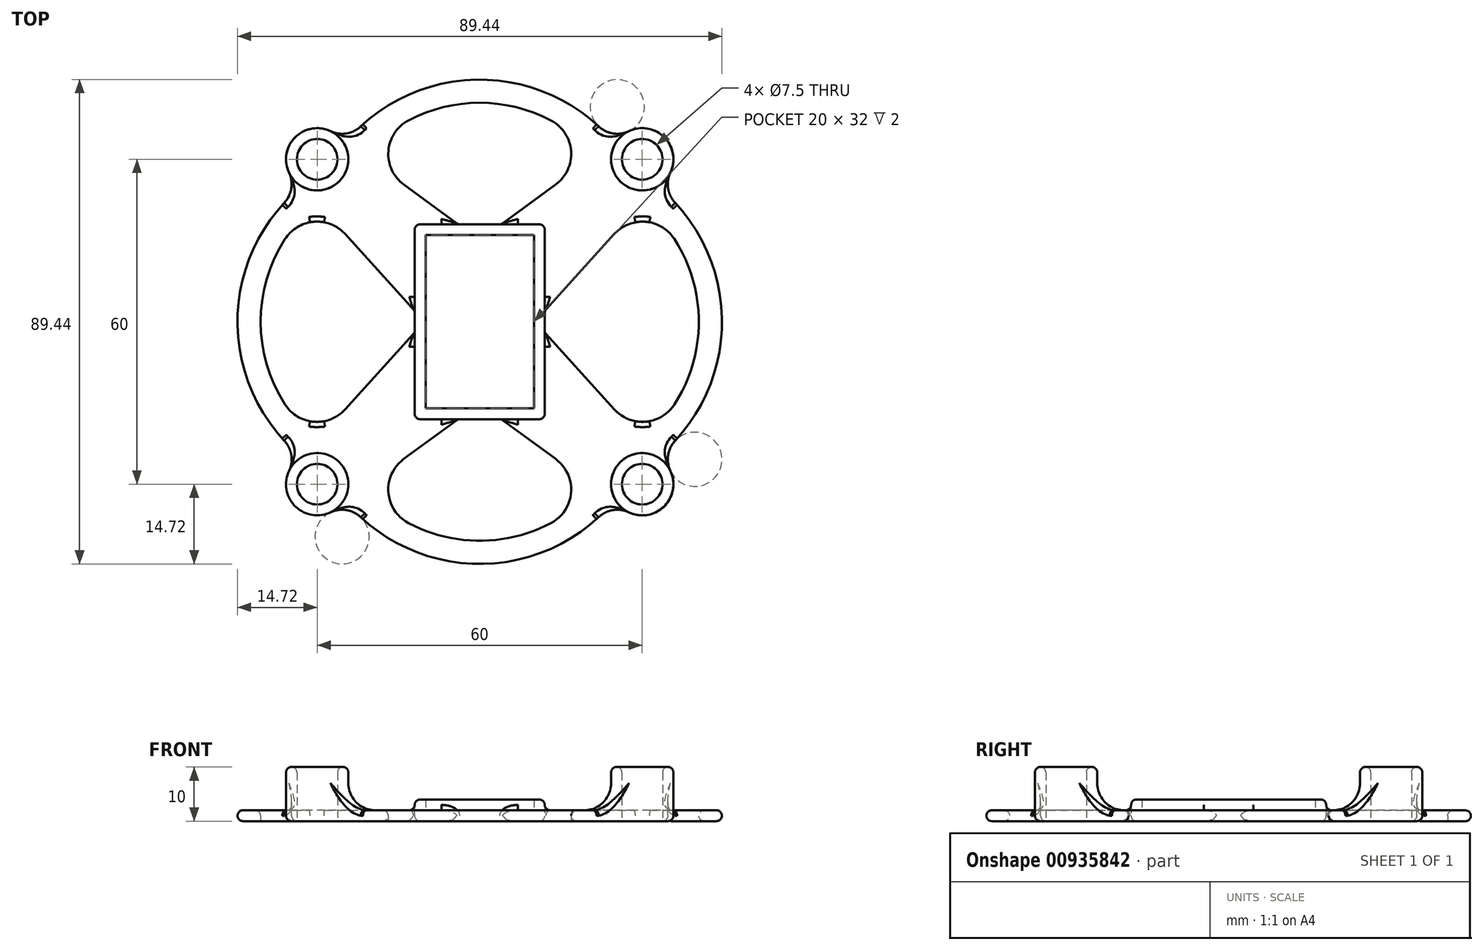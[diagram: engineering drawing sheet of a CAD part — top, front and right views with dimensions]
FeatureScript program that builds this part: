
annotation { "Feature Type Name" : "Feature", "Feature Type Description" : "" }
export const myFeature = defineFeature(function(context is Context, id is Id, definition is map)
    precondition{}
    {
        {
            var Q0;
            Q0=qCreatedBy(makeId("Top.planeOp"),FACE);
            var sketch = newSketch(context, id + "F0", { "sketchPlane" : qUnion([Q0])});
            skLineSegment(sketch, "E0.bottom", {"start": v(-30, -30) * mm, "end": v(30, -30) * mm, "construction": true});
            skLineSegment(sketch, "E0.top", {"start": v(-30, 30) * mm, "end": v(30, 30) * mm, "construction": true});
            skLineSegment(sketch, "E0.left", {"start": v(-30, -30) * mm, "end": v(-30, 30) * mm, "construction": true});
            skLineSegment(sketch, "E0.right", {"start": v(30, -30) * mm, "end": v(30, 30) * mm, "construction": true});
            skPoint(sketch, "E0.middle", {"position": v(0, 0) * mm});
            skCircle(sketch, "E1", {"center": v(-30, 30) * mm, "radius": 3.75 * mm});
            skCircle(sketch, "E2", {"center": v(-30, -30) * mm, "radius": 3.75 * mm});
            skCircle(sketch, "E3", {"center": v(30, -30) * mm, "radius": 3.75 * mm});
            skCircle(sketch, "E4", {"center": v(30, 30) * mm, "radius": 3.75 * mm});
            skCircle(sketch, "E5", {"center": v(-30, 30) * mm, "radius": 5.75 * mm});
            skCircle(sketch, "E6", {"center": v(30, 30) * mm, "radius": 5.75 * mm});
            skCircle(sketch, "E7", {"center": v(30, -30) * mm, "radius": 5.75 * mm});
            skCircle(sketch, "E8", {"center": v(-30, -30) * mm, "radius": 5.75 * mm});
            skLineSegment(sketch, "E9.bottom", {"start": v(10, 16) * mm, "end": v(-10, 16) * mm});
            skLineSegment(sketch, "E9.top", {"start": v(10, -16) * mm, "end": v(-10, -16) * mm});
            skLineSegment(sketch, "E9.left", {"start": v(10, 16) * mm, "end": v(10, -16) * mm});
            skLineSegment(sketch, "E9.right", {"start": v(-10, 16) * mm, "end": v(-10, -16) * mm});
            skLineSegment(sketch, "E10.bottom", {"start": v(12, 18) * mm, "end": v(-12, 18) * mm});
            skLineSegment(sketch, "E10.top", {"start": v(12, -18) * mm, "end": v(-12, -18) * mm});
            skLineSegment(sketch, "E10.left", {"start": v(12, 18) * mm, "end": v(12, -18) * mm});
            skLineSegment(sketch, "E10.right", {"start": v(-12, 18) * mm, "end": v(-12, -18) * mm});
            skLineSegment(sketch, "E11", {"start": v(-26, 34.13) * mm, "end": v(-4, 18) * mm});
            skLineSegment(sketch, "E12", {"start": v(-32.84, 25) * mm, "end": v(-12, 2) * mm});
            skLineSegment(sketch, "E13.MirrorCS", {"start": v(26, 34.13) * mm, "end": v(4, 18) * mm});
            skLineSegment(sketch, "E14.MirrorCS", {"start": v(32.84, 25) * mm, "end": v(12, 2) * mm});
            skLineSegment(sketch, "E15.MirrorCS", {"start": v(-32.84, -25) * mm, "end": v(-12, -2) * mm});
            skLineSegment(sketch, "E16.MirrorCS", {"start": v(-26, -34.13) * mm, "end": v(-4, -18) * mm});
            skLineSegment(sketch, "E17.MirrorCS", {"start": v(26, -34.13) * mm, "end": v(4, -18) * mm});
            skLineSegment(sketch, "E18.MirrorCS", {"start": v(32.84, -25) * mm, "end": v(12, -2) * mm});
            skArc(sketch, "E19", {"start": v(32.84, -25) * mm, "mid": v(44.72, 0) * mm, "end": v(32.84, 25) * mm});
            skArc(sketch, "E20", {"start": v(30, -21.87) * mm, "mid": v(40.44, 0) * mm, "end": v(30, 21.87) * mm});
            skArc(sketch, "E21.1.0", {"start": v(21.87, 30) * mm, "mid": v(0, 40.44) * mm, "end": v(-21.87, 30) * mm});
            skArc(sketch, "E21.1.1", {"start": v(25, 32.84) * mm, "mid": v(0, 44.72) * mm, "end": v(-25, 32.84) * mm});
            skArc(sketch, "E21.2.0", {"start": v(-30, 21.87) * mm, "mid": v(-40.44, 0) * mm, "end": v(-30, -21.87) * mm});
            skArc(sketch, "E21.2.1", {"start": v(-32.84, 25) * mm, "mid": v(-44.72, 0) * mm, "end": v(-32.84, -25) * mm});
            skArc(sketch, "E21.3.0", {"start": v(-21.87, -30) * mm, "mid": v(0, -40.44) * mm, "end": v(21.87, -30) * mm});
            skArc(sketch, "E21.3.1", {"start": v(-25, -32.84) * mm, "mid": v(0, -44.72) * mm, "end": v(25, -32.84) * mm});
            skSolve(sketch);
        }
        {
            var Q0;
            {var subQ0=sQuery(id+"F0.wireOp",EDGE,"E11");Q0=makeQuery(id+"F0.imprint","IMPRINT",FACE,{"disambiguationData":[TD([[makeQuery(id+"F0.imprint","IMPRINT",EDGE,{"derivedFrom":subQ0}),-1.0]])]});}
            var Q1;
            Q1=makeQuery(id+"F0.imprint","IMPRINT",FACE,{"disambiguationData":[TD([[makeQuery(id+"F0.imprint","IMPRINT",EDGE,{"derivedFrom":sQuery(id+"F0.wireOp",EDGE,"E2")}),-1.0]])]});
            var Q2;
            Q2=makeQuery(id+"F0.imprint","IMPRINT",FACE,{"disambiguationData":[TD([[makeQuery(id+"F0.imprint","IMPRINT",EDGE,{"derivedFrom":sQuery(id+"F0.wireOp",EDGE,"E9.bottom")}),1.0]])]});
            var Q3;
            {var subQ0=sQuery(id+"F0.wireOp",EDGE,"E17.MirrorCS");Q3=makeQuery(id+"F0.imprint","IMPRINT",FACE,{"disambiguationData":[TD([[makeQuery(id+"F0.imprint","IMPRINT",EDGE,{"derivedFrom":subQ0}),-1.0]])]});}
            var Q4;
            Q4=makeQuery(id+"F0.imprint","IMPRINT",FACE,{"disambiguationData":[TD([[makeQuery(id+"F0.imprint","IMPRINT",EDGE,{"derivedFrom":sQuery(id+"F0.wireOp",EDGE,"E3")}),-1.0]])]});
            var Q5;
            Q5=makeQuery(id+"F0.imprint","IMPRINT",FACE,{"disambiguationData":[TD([[makeQuery(id+"F0.imprint","IMPRINT",EDGE,{"derivedFrom":sQuery(id+"F0.wireOp",EDGE,"E4")}),-1.0]])]});
            var Q6;
            {var subQ0=sQuery(id+"F0.wireOp",EDGE,"E13.MirrorCS");Q6=makeQuery(id+"F0.imprint","IMPRINT",FACE,{"disambiguationData":[TD([[makeQuery(id+"F0.imprint","IMPRINT",EDGE,{"derivedFrom":subQ0}),1.0]])]});}
            var Q7;
            Q7=makeQuery(id+"F0.imprint","IMPRINT",FACE,{"disambiguationData":[TD([[makeQuery(id+"F0.imprint","IMPRINT",EDGE,{"derivedFrom":sQuery(id+"F0.wireOp",EDGE,"E1")}),-1.0]])]});
            var Q8;
            Q8=makeQuery(id+"F0.imprint","IMPRINT",FACE,{"disambiguationData":[TD([[makeQuery(id+"F0.imprint","IMPRINT",EDGE,{"derivedFrom":sQuery(id+"F0.wireOp",EDGE,"E9.bottom")}),-1.0]])]});
            var Q9;
            {var subQ0=sQuery(id+"F0.wireOp",EDGE,"E15.MirrorCS");Q9=makeQuery(id+"F0.imprint","IMPRINT",FACE,{"disambiguationData":[TD([[makeQuery(id+"F0.imprint","IMPRINT",EDGE,{"derivedFrom":subQ0}),-1.0]])]});}
            var Q10;
            {var subQ2=sQuery(id+"F0.wireOp",EDGE,"E21.2.0");Q10=makeQuery(id+"F0.imprint","IMPRINT",FACE,{"disambiguationData":[TD([[makeQuery(id+"F0.imprint","IMPRINT",EDGE,{"derivedFrom":subQ2}),-1.0]])]});}
            var Q11;
            {var subQ0=sQuery(id+"F0.wireOp",EDGE,"E21.3.1");var subQ1=sQuery(id+"F0.wireOp",EDGE,"E16.MirrorCS");var subQ2=makeQuery(id+"F0.imprint","INTERSECT",VERTEX,{"derivedFrom":[subQ1,subQ0]});Q11=makeQuery(id+"F0.imprint","IMPRINT",FACE,{"disambiguationData":[TD([[makeQuery(id+"F0.imprint","IMPRINT",EDGE,{"disambiguationData":[TD([[subQ2,-1.0]])],"derivedFrom":subQ1}),-1.0]])]});}
            var Q12;
            {var subQ0=sQuery(id+"F0.wireOp",EDGE,"E19");Q12=makeQuery(id+"F0.imprint","IMPRINT",FACE,{"disambiguationData":[TD([[makeQuery(id+"F0.imprint","IMPRINT",EDGE,{"derivedFrom":subQ0}),1.0]])]});}
            var Q13;
            {var subQ0=sQuery(id+"F0.wireOp",EDGE,"E21.1.1");var subQ1=sQuery(id+"F0.wireOp",EDGE,"E11");var subQ2=makeQuery(id+"F0.imprint","INTERSECT",VERTEX,{"derivedFrom":[subQ1,subQ0]});Q13=makeQuery(id+"F0.imprint","IMPRINT",FACE,{"disambiguationData":[TD([[makeQuery(id+"F0.imprint","IMPRINT",EDGE,{"disambiguationData":[TD([[subQ2,-1.0]])],"derivedFrom":subQ1}),1.0]])]});}
            extrude(context, id + "F1", {"entities" : qUnion([Q0, Q1, Q2, Q3, Q4, Q5, Q6, Q7, Q8, Q9, Q10, Q11, Q12, Q13]), "depth" : 2 * mm, "offsetDistance" : 25 * mm});
        }
        {
            var Q0;
            Q0=makeQuery(id+"F0.imprint","IMPRINT",FACE,{"disambiguationData":[TD([[makeQuery(id+"F0.imprint","IMPRINT",EDGE,{"derivedFrom":sQuery(id+"F0.wireOp",EDGE,"E4")}),-1.0]])]});
            var Q1;
            Q1=makeQuery(id+"F0.imprint","IMPRINT",FACE,{"disambiguationData":[TD([[makeQuery(id+"F0.imprint","IMPRINT",EDGE,{"derivedFrom":sQuery(id+"F0.wireOp",EDGE,"E3")}),-1.0]])]});
            var Q2;
            Q2=makeQuery(id+"F0.imprint","IMPRINT",FACE,{"disambiguationData":[TD([[makeQuery(id+"F0.imprint","IMPRINT",EDGE,{"derivedFrom":sQuery(id+"F0.wireOp",EDGE,"E1")}),-1.0]])]});
            var Q3;
            Q3=makeQuery(id+"F0.imprint","IMPRINT",FACE,{"disambiguationData":[TD([[makeQuery(id+"F0.imprint","IMPRINT",EDGE,{"derivedFrom":sQuery(id+"F0.wireOp",EDGE,"E2")}),-1.0]])]});
            extrude(context, id + "F2", {"entities" : qUnion([Q0, Q1, Q2, Q3]), "operationType" : NewBodyOperationType.ADD, "depth" : 10 * mm, "offsetDistance" : 25 * mm});
        }
        {
            var Q0;
            Q0=makeQuery(id+"F0.imprint","IMPRINT",FACE,{"disambiguationData":[TD([[makeQuery(id+"F0.imprint","IMPRINT",EDGE,{"derivedFrom":sQuery(id+"F0.wireOp",EDGE,"E9.bottom")}),-1.0]])]});
            extrude(context, id + "F3", {"entities" : qUnion([Q0]), "operationType" : NewBodyOperationType.ADD, "depth" : 4 * mm, "offsetDistance" : 25 * mm});
        }
        {
            var Q0;
            Q0=makeQuery(id+"F1.opExtrude","SWEPT_EDGE",EDGE,{"disambiguationData":[OSD([sQuery(id+"F0.wireOp",EDGE,"E14.MirrorCS"),sQuery(id+"F0.wireOp",EDGE,"E20")])]});
            var Q1;
            Q1=makeQuery(id+"F1.opExtrude","SWEPT_EDGE",EDGE,{"disambiguationData":[OSD([sQuery(id+"F0.wireOp",EDGE,"E18.MirrorCS"),sQuery(id+"F0.wireOp",EDGE,"E20")])]});
            var Q2;
            Q2=makeQuery(id+"F1.opExtrude","SWEPT_EDGE",EDGE,{"disambiguationData":[OSD([sQuery(id+"F0.wireOp",EDGE,"E17.MirrorCS"),sQuery(id+"F0.wireOp",EDGE,"E21.3.0")])]});
            var Q3;
            Q3=makeQuery(id+"F1.opExtrude","SWEPT_EDGE",EDGE,{"disambiguationData":[OSD([sQuery(id+"F0.wireOp",EDGE,"E16.MirrorCS"),sQuery(id+"F0.wireOp",EDGE,"E21.3.0")])]});
            var Q4;
            Q4=makeQuery(id+"F1.opExtrude","SWEPT_EDGE",EDGE,{"disambiguationData":[OSD([sQuery(id+"F0.wireOp",EDGE,"E12"),sQuery(id+"F0.wireOp",EDGE,"E21.2.0")])]});
            var Q5;
            Q5=makeQuery(id+"F1.opExtrude","SWEPT_EDGE",EDGE,{"disambiguationData":[OSD([sQuery(id+"F0.wireOp",EDGE,"E15.MirrorCS"),sQuery(id+"F0.wireOp",EDGE,"E21.2.0")])]});
            var Q6;
            Q6=makeQuery(id+"F1.opExtrude","SWEPT_EDGE",EDGE,{"disambiguationData":[OSD([sQuery(id+"F0.wireOp",EDGE,"E11"),sQuery(id+"F0.wireOp",EDGE,"E21.1.0")])]});
            var Q7;
            Q7=makeQuery(id+"F1.opExtrude","SWEPT_EDGE",EDGE,{"disambiguationData":[OSD([sQuery(id+"F0.wireOp",EDGE,"E13.MirrorCS"),sQuery(id+"F0.wireOp",EDGE,"E21.1.0")])]});
            fillet(context, id + "F4", {"entities" : qUnion([Q0, Q1, Q2, Q3, Q4, Q5, Q6, Q7]), "radius" : 7 * mm, "tangentPropagation" : true, "allowEdgeOverflow" : false});
        }
        {
            var Q0;
            {var subQ0=sQuery(id+"F0.wireOp",EDGE,"E5");Q0=makeQuery(id+"F2.boolean.opBoolean","INTERSECT",EDGE,{"derivedFrom":[makeQuery(id+"F1.opExtrude","CAP_FACE",FACE,{"disambiguationData":[OSD([sQuery(id+"F0.wireOp",EDGE,"E1"),sQuery(id+"F0.wireOp",EDGE,"E2"),sQuery(id+"F0.wireOp",EDGE,"E3"),sQuery(id+"F0.wireOp",EDGE,"E4"),subQ0,sQuery(id+"F0.wireOp",EDGE,"E6"),sQuery(id+"F0.wireOp",EDGE,"E7"),sQuery(id+"F0.wireOp",EDGE,"E8"),sQuery(id+"F0.wireOp",EDGE,"E10.bottom"),sQuery(id+"F0.wireOp",EDGE,"E10.top"),sQuery(id+"F0.wireOp",EDGE,"E10.left"),sQuery(id+"F0.wireOp",EDGE,"E10.right"),sQuery(id+"F0.wireOp",EDGE,"E11"),sQuery(id+"F0.wireOp",EDGE,"E12"),sQuery(id+"F0.wireOp",EDGE,"E13.MirrorCS"),sQuery(id+"F0.wireOp",EDGE,"E14.MirrorCS"),sQuery(id+"F0.wireOp",EDGE,"E15.MirrorCS"),sQuery(id+"F0.wireOp",EDGE,"E16.MirrorCS"),sQuery(id+"F0.wireOp",EDGE,"E17.MirrorCS"),sQuery(id+"F0.wireOp",EDGE,"E18.MirrorCS"),sQuery(id+"F0.wireOp",EDGE,"E19"),sQuery(id+"F0.wireOp",EDGE,"E20"),sQuery(id+"F0.wireOp",EDGE,"E21.1.0"),sQuery(id+"F0.wireOp",EDGE,"E21.1.1"),sQuery(id+"F0.wireOp",EDGE,"E21.2.0"),sQuery(id+"F0.wireOp",EDGE,"E21.2.1"),sQuery(id+"F0.wireOp",EDGE,"E21.3.0"),sQuery(id+"F0.wireOp",EDGE,"E21.3.1")])],"isStart":false}),makeQuery(id+"F2.opExtrude","SWEPT_FACE",FACE,{"disambiguationData":[OSD([subQ0])]})]});}
            var Q1;
            {var subQ0=sQuery(id+"F0.wireOp",EDGE,"E6");Q1=makeQuery(id+"F2.boolean.opBoolean","INTERSECT",EDGE,{"derivedFrom":[makeQuery(id+"F1.opExtrude","CAP_FACE",FACE,{"disambiguationData":[OSD([sQuery(id+"F0.wireOp",EDGE,"E1"),sQuery(id+"F0.wireOp",EDGE,"E2"),sQuery(id+"F0.wireOp",EDGE,"E3"),sQuery(id+"F0.wireOp",EDGE,"E4"),sQuery(id+"F0.wireOp",EDGE,"E5"),subQ0,sQuery(id+"F0.wireOp",EDGE,"E7"),sQuery(id+"F0.wireOp",EDGE,"E8"),sQuery(id+"F0.wireOp",EDGE,"E10.bottom"),sQuery(id+"F0.wireOp",EDGE,"E10.top"),sQuery(id+"F0.wireOp",EDGE,"E10.left"),sQuery(id+"F0.wireOp",EDGE,"E10.right"),sQuery(id+"F0.wireOp",EDGE,"E11"),sQuery(id+"F0.wireOp",EDGE,"E12"),sQuery(id+"F0.wireOp",EDGE,"E13.MirrorCS"),sQuery(id+"F0.wireOp",EDGE,"E14.MirrorCS"),sQuery(id+"F0.wireOp",EDGE,"E15.MirrorCS"),sQuery(id+"F0.wireOp",EDGE,"E16.MirrorCS"),sQuery(id+"F0.wireOp",EDGE,"E17.MirrorCS"),sQuery(id+"F0.wireOp",EDGE,"E18.MirrorCS"),sQuery(id+"F0.wireOp",EDGE,"E19"),sQuery(id+"F0.wireOp",EDGE,"E20"),sQuery(id+"F0.wireOp",EDGE,"E21.1.0"),sQuery(id+"F0.wireOp",EDGE,"E21.1.1"),sQuery(id+"F0.wireOp",EDGE,"E21.2.0"),sQuery(id+"F0.wireOp",EDGE,"E21.2.1"),sQuery(id+"F0.wireOp",EDGE,"E21.3.0"),sQuery(id+"F0.wireOp",EDGE,"E21.3.1")])],"isStart":false}),makeQuery(id+"F2.opExtrude","SWEPT_FACE",FACE,{"disambiguationData":[OSD([subQ0])]})]});}
            var Q2;
            {var subQ0=sQuery(id+"F0.wireOp",EDGE,"E8");Q2=makeQuery(id+"F2.boolean.opBoolean","INTERSECT",EDGE,{"derivedFrom":[makeQuery(id+"F1.opExtrude","CAP_FACE",FACE,{"disambiguationData":[OSD([sQuery(id+"F0.wireOp",EDGE,"E1"),sQuery(id+"F0.wireOp",EDGE,"E2"),sQuery(id+"F0.wireOp",EDGE,"E3"),sQuery(id+"F0.wireOp",EDGE,"E4"),sQuery(id+"F0.wireOp",EDGE,"E5"),sQuery(id+"F0.wireOp",EDGE,"E6"),sQuery(id+"F0.wireOp",EDGE,"E7"),subQ0,sQuery(id+"F0.wireOp",EDGE,"E10.bottom"),sQuery(id+"F0.wireOp",EDGE,"E10.top"),sQuery(id+"F0.wireOp",EDGE,"E10.left"),sQuery(id+"F0.wireOp",EDGE,"E10.right"),sQuery(id+"F0.wireOp",EDGE,"E11"),sQuery(id+"F0.wireOp",EDGE,"E12"),sQuery(id+"F0.wireOp",EDGE,"E13.MirrorCS"),sQuery(id+"F0.wireOp",EDGE,"E14.MirrorCS"),sQuery(id+"F0.wireOp",EDGE,"E15.MirrorCS"),sQuery(id+"F0.wireOp",EDGE,"E16.MirrorCS"),sQuery(id+"F0.wireOp",EDGE,"E17.MirrorCS"),sQuery(id+"F0.wireOp",EDGE,"E18.MirrorCS"),sQuery(id+"F0.wireOp",EDGE,"E19"),sQuery(id+"F0.wireOp",EDGE,"E20"),sQuery(id+"F0.wireOp",EDGE,"E21.1.0"),sQuery(id+"F0.wireOp",EDGE,"E21.1.1"),sQuery(id+"F0.wireOp",EDGE,"E21.2.0"),sQuery(id+"F0.wireOp",EDGE,"E21.2.1"),sQuery(id+"F0.wireOp",EDGE,"E21.3.0"),sQuery(id+"F0.wireOp",EDGE,"E21.3.1")])],"isStart":false}),makeQuery(id+"F2.opExtrude","SWEPT_FACE",FACE,{"disambiguationData":[OSD([subQ0])]})]});}
            var Q3;
            {var subQ0=sQuery(id+"F0.wireOp",EDGE,"E7");Q3=makeQuery(id+"F2.boolean.opBoolean","INTERSECT",EDGE,{"derivedFrom":[makeQuery(id+"F1.opExtrude","CAP_FACE",FACE,{"disambiguationData":[OSD([sQuery(id+"F0.wireOp",EDGE,"E1"),sQuery(id+"F0.wireOp",EDGE,"E2"),sQuery(id+"F0.wireOp",EDGE,"E3"),sQuery(id+"F0.wireOp",EDGE,"E4"),sQuery(id+"F0.wireOp",EDGE,"E5"),sQuery(id+"F0.wireOp",EDGE,"E6"),subQ0,sQuery(id+"F0.wireOp",EDGE,"E8"),sQuery(id+"F0.wireOp",EDGE,"E10.bottom"),sQuery(id+"F0.wireOp",EDGE,"E10.top"),sQuery(id+"F0.wireOp",EDGE,"E10.left"),sQuery(id+"F0.wireOp",EDGE,"E10.right"),sQuery(id+"F0.wireOp",EDGE,"E11"),sQuery(id+"F0.wireOp",EDGE,"E12"),sQuery(id+"F0.wireOp",EDGE,"E13.MirrorCS"),sQuery(id+"F0.wireOp",EDGE,"E14.MirrorCS"),sQuery(id+"F0.wireOp",EDGE,"E15.MirrorCS"),sQuery(id+"F0.wireOp",EDGE,"E16.MirrorCS"),sQuery(id+"F0.wireOp",EDGE,"E17.MirrorCS"),sQuery(id+"F0.wireOp",EDGE,"E18.MirrorCS"),sQuery(id+"F0.wireOp",EDGE,"E19"),sQuery(id+"F0.wireOp",EDGE,"E20"),sQuery(id+"F0.wireOp",EDGE,"E21.1.0"),sQuery(id+"F0.wireOp",EDGE,"E21.1.1"),sQuery(id+"F0.wireOp",EDGE,"E21.2.0"),sQuery(id+"F0.wireOp",EDGE,"E21.2.1"),sQuery(id+"F0.wireOp",EDGE,"E21.3.0"),sQuery(id+"F0.wireOp",EDGE,"E21.3.1")])],"isStart":false}),makeQuery(id+"F2.opExtrude","SWEPT_FACE",FACE,{"disambiguationData":[OSD([subQ0])]})]});}
            fillet(context, id + "F5", {"entities" : qUnion([Q0, Q1, Q2, Q3]), "radius" : 5 * mm, "tangentPropagation" : true, "allowEdgeOverflow" : false});
        }
        {
            var Q0;
            Q0=makeQuery(id+"F1.opExtrude","SWEPT_EDGE",EDGE,{"disambiguationData":[OSD([sQuery(id+"F0.wireOp",EDGE,"E5"),sQuery(id+"F0.wireOp",EDGE,"E12"),sQuery(id+"F0.wireOp",EDGE,"E21.2.1")])]});
            var Q1;
            Q1=makeQuery(id+"F1.opExtrude","SWEPT_EDGE",EDGE,{"disambiguationData":[OSD([sQuery(id+"F0.wireOp",EDGE,"E5"),sQuery(id+"F0.wireOp",EDGE,"E21.1.1")])]});
            var Q2;
            Q2=makeQuery(id+"F1.opExtrude","SWEPT_EDGE",EDGE,{"disambiguationData":[OSD([sQuery(id+"F0.wireOp",EDGE,"E6"),sQuery(id+"F0.wireOp",EDGE,"E21.1.1")])]});
            var Q3;
            Q3=makeQuery(id+"F1.opExtrude","SWEPT_EDGE",EDGE,{"disambiguationData":[OSD([sQuery(id+"F0.wireOp",EDGE,"E6"),sQuery(id+"F0.wireOp",EDGE,"E14.MirrorCS"),sQuery(id+"F0.wireOp",EDGE,"E19")])]});
            var Q4;
            Q4=makeQuery(id+"F1.opExtrude","SWEPT_EDGE",EDGE,{"disambiguationData":[OSD([sQuery(id+"F0.wireOp",EDGE,"E7"),sQuery(id+"F0.wireOp",EDGE,"E18.MirrorCS"),sQuery(id+"F0.wireOp",EDGE,"E19")])]});
            var Q5;
            Q5=makeQuery(id+"F1.opExtrude","SWEPT_EDGE",EDGE,{"disambiguationData":[OSD([sQuery(id+"F0.wireOp",EDGE,"E7"),sQuery(id+"F0.wireOp",EDGE,"E21.3.1")])]});
            var Q6;
            Q6=makeQuery(id+"F1.opExtrude","SWEPT_EDGE",EDGE,{"disambiguationData":[OSD([sQuery(id+"F0.wireOp",EDGE,"E8"),sQuery(id+"F0.wireOp",EDGE,"E21.3.1")])]});
            var Q7;
            Q7=makeQuery(id+"F1.opExtrude","SWEPT_EDGE",EDGE,{"disambiguationData":[OSD([sQuery(id+"F0.wireOp",EDGE,"E8"),sQuery(id+"F0.wireOp",EDGE,"E15.MirrorCS"),sQuery(id+"F0.wireOp",EDGE,"E21.2.1")])]});
            fillet(context, id + "F6", {"entities" : qUnion([Q0, Q1, Q2, Q3, Q4, Q5, Q6, Q7]), "radius" : 5 * mm, "tangentPropagation" : true, "allowEdgeOverflow" : false});
        }
        {
            var Q0;
            Q0=makeQuery(id+"F1.opExtrude","CAP_EDGE",EDGE,{"disambiguationData":[OSD([sQuery(id+"F0.wireOp",EDGE,"E10.top")])],"isStart":true});
            var Q1;
            {var subQ0=sQuery(id+"F0.wireOp",EDGE,"E10.top");Q1=makeQuery(id+"F3.boolean.opBoolean","MERGE",FACE,{"derivedFrom":[makeQuery(id+"F1.opExtrude","SWEPT_FACE",FACE,{"disambiguationData":[OSD([subQ0])]}),makeQuery(id+"F3.opExtrude","SWEPT_FACE",FACE,{"disambiguationData":[OSD([subQ0])]})]});}
            var Q2;
            {var subQ0=sQuery(id+"F0.wireOp",EDGE,"E10.bottom");Q2=makeQuery(id+"F3.boolean.opBoolean","MERGE",FACE,{"derivedFrom":[makeQuery(id+"F1.opExtrude","SWEPT_FACE",FACE,{"disambiguationData":[OSD([subQ0])]}),makeQuery(id+"F3.opExtrude","SWEPT_FACE",FACE,{"disambiguationData":[OSD([subQ0])]})]});}
            var Q3;
            {var subQ0=sQuery(id+"F0.wireOp",EDGE,"E10.right");Q3=makeQuery(id+"F3.boolean.opBoolean","MERGE",FACE,{"derivedFrom":[makeQuery(id+"F1.opExtrude","SWEPT_FACE",FACE,{"disambiguationData":[OSD([subQ0])]}),makeQuery(id+"F3.opExtrude","SWEPT_FACE",FACE,{"disambiguationData":[OSD([subQ0])]})]});}
            var Q4;
            {var subQ0=sQuery(id+"F0.wireOp",EDGE,"E10.left");Q4=makeQuery(id+"F3.boolean.opBoolean","MERGE",FACE,{"derivedFrom":[makeQuery(id+"F1.opExtrude","SWEPT_FACE",FACE,{"disambiguationData":[OSD([subQ0])]}),makeQuery(id+"F3.opExtrude","SWEPT_FACE",FACE,{"disambiguationData":[OSD([subQ0])]})]});}
            var Q5;
            Q5=makeQuery(id+"F1.opExtrude","CAP_EDGE",EDGE,{"disambiguationData":[OSD([sQuery(id+"F0.wireOp",EDGE,"E21.1.1")])],"isStart":true});
            var Q6;
            Q6=makeQuery(id+"F1.opExtrude","CAP_EDGE",EDGE,{"disambiguationData":[OSD([sQuery(id+"F0.wireOp",EDGE,"E21.1.1")])],"isStart":false});
            var Q7;
            Q7=makeQuery(id+"F1.opExtrude","CAP_EDGE",EDGE,{"disambiguationData":[OSD([sQuery(id+"F0.wireOp",EDGE,"E19")])],"isStart":false});
            var Q8;
            Q8=makeQuery(id+"F1.opExtrude","CAP_EDGE",EDGE,{"disambiguationData":[OSD([sQuery(id+"F0.wireOp",EDGE,"E19")])],"isStart":true});
            var Q9;
            Q9=makeQuery(id+"F1.opExtrude","CAP_EDGE",EDGE,{"disambiguationData":[OSD([sQuery(id+"F0.wireOp",EDGE,"E21.3.1")])],"isStart":false});
            var Q10;
            Q10=makeQuery(id+"F1.opExtrude","CAP_EDGE",EDGE,{"disambiguationData":[OSD([sQuery(id+"F0.wireOp",EDGE,"E21.3.1")])],"isStart":true});
            var Q11;
            Q11=makeQuery(id+"F1.opExtrude","CAP_EDGE",EDGE,{"disambiguationData":[OSD([sQuery(id+"F0.wireOp",EDGE,"E21.2.1")])],"isStart":true});
            var Q12;
            Q12=makeQuery(id+"F1.opExtrude","CAP_EDGE",EDGE,{"disambiguationData":[OSD([sQuery(id+"F0.wireOp",EDGE,"E21.2.1")])],"isStart":false});
            var Q13;
            {var subQ0=sQuery(id+"F0.wireOp",EDGE,"E21.2.1");var subQ1=sQuery(id+"F0.wireOp",EDGE,"E21.2.0");var subQ2=sQuery(id+"F0.wireOp",EDGE,"E21.1.1");var subQ3=sQuery(id+"F0.wireOp",EDGE,"E21.1.0");var subQ4=sQuery(id+"F0.wireOp",EDGE,"E20");var subQ5=sQuery(id+"F0.wireOp",EDGE,"E19");var subQ6=sQuery(id+"F0.wireOp",EDGE,"E18.MirrorCS");var subQ7=sQuery(id+"F0.wireOp",EDGE,"E17.MirrorCS");var subQ8=sQuery(id+"F0.wireOp",EDGE,"E16.MirrorCS");var subQ9=sQuery(id+"F0.wireOp",EDGE,"E15.MirrorCS");var subQ10=sQuery(id+"F0.wireOp",EDGE,"E14.MirrorCS");var subQ11=sQuery(id+"F0.wireOp",EDGE,"E13.MirrorCS");var subQ12=sQuery(id+"F0.wireOp",EDGE,"E8");var subQ13=sQuery(id+"F0.wireOp",EDGE,"E7");var subQ14=sQuery(id+"F0.wireOp",EDGE,"E6");var subQ15=sQuery(id+"F0.wireOp",EDGE,"E5");var subQ16=sQuery(id+"F0.wireOp",EDGE,"E10.bottom");var subQ17=sQuery(id+"F0.wireOp",EDGE,"E10.top");var subQ18=sQuery(id+"F0.wireOp",EDGE,"E10.left");var subQ19=sQuery(id+"F0.wireOp",EDGE,"E10.right");var subQ20=sQuery(id+"F0.wireOp",EDGE,"E11");var subQ21=sQuery(id+"F0.wireOp",EDGE,"E12");var subQ22=sQuery(id+"F0.wireOp",EDGE,"E21.3.0");var subQ23=sQuery(id+"F0.wireOp",EDGE,"E21.3.1");Q13=makeQuery(id+"F4.opFillet","BLEND_EDGE",EDGE,{"blendedFrom":[makeQuery(id+"F1.opExtrude","SWEPT_EDGE",EDGE,{"disambiguationData":[OSD([subQ20,subQ3])]}),makeQuery(id+"F3.boolean.opBoolean","SPLIT",FACE,{"disambiguationData":[TD([makeQuery(id+"F1.opExtrude","SWEPT_FACE",FACE,{"disambiguationData":[OSD([subQ15])]})])],"derivedFrom":makeQuery(id+"F1.opExtrude","CAP_FACE",FACE,{"disambiguationData":[OSD([sQuery(id+"F0.wireOp",EDGE,"E1"),sQuery(id+"F0.wireOp",EDGE,"E2"),sQuery(id+"F0.wireOp",EDGE,"E3"),sQuery(id+"F0.wireOp",EDGE,"E4"),subQ15,subQ14,subQ13,subQ12,subQ16,subQ17,subQ18,subQ19,subQ20,subQ21,subQ11,subQ10,subQ9,subQ8,subQ7,subQ6,subQ5,subQ4,subQ3,subQ2,subQ1,subQ0,subQ22,subQ23])],"isStart":false})})],"blendedInto":[makeQuery(id+"F3.boolean.opBoolean","SPLIT",FACE,{"disambiguationData":[TD([makeQuery(id+"F1.opExtrude","SWEPT_FACE",FACE,{"disambiguationData":[OSD([subQ15])]})])],"derivedFrom":makeQuery(id+"F1.opExtrude","CAP_FACE",FACE,{"disambiguationData":[OSD([sQuery(id+"F0.wireOp",EDGE,"E1"),sQuery(id+"F0.wireOp",EDGE,"E2"),sQuery(id+"F0.wireOp",EDGE,"E3"),sQuery(id+"F0.wireOp",EDGE,"E4"),subQ15,subQ14,subQ13,subQ12,subQ16,subQ17,subQ18,subQ19,subQ20,subQ21,subQ11,subQ10,subQ9,subQ8,subQ7,subQ6,subQ5,subQ4,subQ3,subQ2,subQ1,subQ0,subQ22,subQ23])],"isStart":false})})]});}
            var Q14;
            Q14=makeQuery(id+"F1.opExtrude","CAP_EDGE",EDGE,{"disambiguationData":[OSD([sQuery(id+"F0.wireOp",EDGE,"E11")])],"isStart":false});
            var Q15;
            Q15=makeQuery(id+"F1.opExtrude","CAP_EDGE",EDGE,{"disambiguationData":[OSD([sQuery(id+"F0.wireOp",EDGE,"E12")])],"isStart":false});
            var Q16;
            {var subQ0=sQuery(id+"F0.wireOp",EDGE,"E21.2.1");var subQ1=sQuery(id+"F0.wireOp",EDGE,"E21.2.0");var subQ2=sQuery(id+"F0.wireOp",EDGE,"E21.1.1");var subQ3=sQuery(id+"F0.wireOp",EDGE,"E21.1.0");var subQ4=sQuery(id+"F0.wireOp",EDGE,"E20");var subQ5=sQuery(id+"F0.wireOp",EDGE,"E19");var subQ6=sQuery(id+"F0.wireOp",EDGE,"E18.MirrorCS");var subQ7=sQuery(id+"F0.wireOp",EDGE,"E17.MirrorCS");var subQ8=sQuery(id+"F0.wireOp",EDGE,"E16.MirrorCS");var subQ9=sQuery(id+"F0.wireOp",EDGE,"E15.MirrorCS");var subQ10=sQuery(id+"F0.wireOp",EDGE,"E14.MirrorCS");var subQ11=sQuery(id+"F0.wireOp",EDGE,"E13.MirrorCS");var subQ12=sQuery(id+"F0.wireOp",EDGE,"E8");var subQ13=sQuery(id+"F0.wireOp",EDGE,"E7");var subQ14=sQuery(id+"F0.wireOp",EDGE,"E6");var subQ15=sQuery(id+"F0.wireOp",EDGE,"E5");var subQ16=sQuery(id+"F0.wireOp",EDGE,"E10.bottom");var subQ17=sQuery(id+"F0.wireOp",EDGE,"E10.top");var subQ18=sQuery(id+"F0.wireOp",EDGE,"E10.left");var subQ19=sQuery(id+"F0.wireOp",EDGE,"E10.right");var subQ20=sQuery(id+"F0.wireOp",EDGE,"E11");var subQ21=sQuery(id+"F0.wireOp",EDGE,"E12");var subQ22=sQuery(id+"F0.wireOp",EDGE,"E21.3.0");var subQ23=sQuery(id+"F0.wireOp",EDGE,"E21.3.1");Q16=makeQuery(id+"F4.opFillet","BLEND_EDGE",EDGE,{"blendedFrom":[makeQuery(id+"F1.opExtrude","SWEPT_EDGE",EDGE,{"disambiguationData":[OSD([subQ21,subQ1])]}),makeQuery(id+"F3.boolean.opBoolean","SPLIT",FACE,{"disambiguationData":[TD([makeQuery(id+"F1.opExtrude","SWEPT_FACE",FACE,{"disambiguationData":[OSD([subQ15])]})])],"derivedFrom":makeQuery(id+"F1.opExtrude","CAP_FACE",FACE,{"disambiguationData":[OSD([sQuery(id+"F0.wireOp",EDGE,"E1"),sQuery(id+"F0.wireOp",EDGE,"E2"),sQuery(id+"F0.wireOp",EDGE,"E3"),sQuery(id+"F0.wireOp",EDGE,"E4"),subQ15,subQ14,subQ13,subQ12,subQ16,subQ17,subQ18,subQ19,subQ20,subQ21,subQ11,subQ10,subQ9,subQ8,subQ7,subQ6,subQ5,subQ4,subQ3,subQ2,subQ1,subQ0,subQ22,subQ23])],"isStart":false})})],"blendedInto":[makeQuery(id+"F3.boolean.opBoolean","SPLIT",FACE,{"disambiguationData":[TD([makeQuery(id+"F1.opExtrude","SWEPT_FACE",FACE,{"disambiguationData":[OSD([subQ15])]})])],"derivedFrom":makeQuery(id+"F1.opExtrude","CAP_FACE",FACE,{"disambiguationData":[OSD([sQuery(id+"F0.wireOp",EDGE,"E1"),sQuery(id+"F0.wireOp",EDGE,"E2"),sQuery(id+"F0.wireOp",EDGE,"E3"),sQuery(id+"F0.wireOp",EDGE,"E4"),subQ15,subQ14,subQ13,subQ12,subQ16,subQ17,subQ18,subQ19,subQ20,subQ21,subQ11,subQ10,subQ9,subQ8,subQ7,subQ6,subQ5,subQ4,subQ3,subQ2,subQ1,subQ0,subQ22,subQ23])],"isStart":false})})]});}
            var Q17;
            Q17=makeQuery(id+"F1.opExtrude","CAP_EDGE",EDGE,{"disambiguationData":[OSD([sQuery(id+"F0.wireOp",EDGE,"E16.MirrorCS")])],"isStart":false});
            var Q18;
            {var subQ0=sQuery(id+"F0.wireOp",EDGE,"E21.2.1");var subQ1=sQuery(id+"F0.wireOp",EDGE,"E21.2.0");var subQ2=sQuery(id+"F0.wireOp",EDGE,"E21.1.1");var subQ3=sQuery(id+"F0.wireOp",EDGE,"E21.1.0");var subQ4=sQuery(id+"F0.wireOp",EDGE,"E20");var subQ5=sQuery(id+"F0.wireOp",EDGE,"E19");var subQ6=sQuery(id+"F0.wireOp",EDGE,"E18.MirrorCS");var subQ7=sQuery(id+"F0.wireOp",EDGE,"E17.MirrorCS");var subQ8=sQuery(id+"F0.wireOp",EDGE,"E16.MirrorCS");var subQ9=sQuery(id+"F0.wireOp",EDGE,"E15.MirrorCS");var subQ10=sQuery(id+"F0.wireOp",EDGE,"E14.MirrorCS");var subQ11=sQuery(id+"F0.wireOp",EDGE,"E13.MirrorCS");var subQ12=sQuery(id+"F0.wireOp",EDGE,"E8");var subQ13=sQuery(id+"F0.wireOp",EDGE,"E7");var subQ14=sQuery(id+"F0.wireOp",EDGE,"E6");var subQ15=sQuery(id+"F0.wireOp",EDGE,"E5");var subQ16=sQuery(id+"F0.wireOp",EDGE,"E10.bottom");var subQ17=sQuery(id+"F0.wireOp",EDGE,"E10.top");var subQ18=sQuery(id+"F0.wireOp",EDGE,"E10.left");var subQ19=sQuery(id+"F0.wireOp",EDGE,"E10.right");var subQ20=sQuery(id+"F0.wireOp",EDGE,"E11");var subQ21=sQuery(id+"F0.wireOp",EDGE,"E12");var subQ22=sQuery(id+"F0.wireOp",EDGE,"E21.3.0");var subQ23=sQuery(id+"F0.wireOp",EDGE,"E21.3.1");Q18=makeQuery(id+"F4.opFillet","BLEND_EDGE",EDGE,{"blendedFrom":[makeQuery(id+"F1.opExtrude","SWEPT_EDGE",EDGE,{"disambiguationData":[OSD([subQ8,subQ22])]}),makeQuery(id+"F3.boolean.opBoolean","SPLIT",FACE,{"disambiguationData":[TD([makeQuery(id+"F1.opExtrude","SWEPT_FACE",FACE,{"disambiguationData":[OSD([subQ15])]})])],"derivedFrom":makeQuery(id+"F1.opExtrude","CAP_FACE",FACE,{"disambiguationData":[OSD([sQuery(id+"F0.wireOp",EDGE,"E1"),sQuery(id+"F0.wireOp",EDGE,"E2"),sQuery(id+"F0.wireOp",EDGE,"E3"),sQuery(id+"F0.wireOp",EDGE,"E4"),subQ15,subQ14,subQ13,subQ12,subQ16,subQ17,subQ18,subQ19,subQ20,subQ21,subQ11,subQ10,subQ9,subQ8,subQ7,subQ6,subQ5,subQ4,subQ3,subQ2,subQ1,subQ0,subQ22,subQ23])],"isStart":false})})],"blendedInto":[makeQuery(id+"F3.boolean.opBoolean","SPLIT",FACE,{"disambiguationData":[TD([makeQuery(id+"F1.opExtrude","SWEPT_FACE",FACE,{"disambiguationData":[OSD([subQ15])]})])],"derivedFrom":makeQuery(id+"F1.opExtrude","CAP_FACE",FACE,{"disambiguationData":[OSD([sQuery(id+"F0.wireOp",EDGE,"E1"),sQuery(id+"F0.wireOp",EDGE,"E2"),sQuery(id+"F0.wireOp",EDGE,"E3"),sQuery(id+"F0.wireOp",EDGE,"E4"),subQ15,subQ14,subQ13,subQ12,subQ16,subQ17,subQ18,subQ19,subQ20,subQ21,subQ11,subQ10,subQ9,subQ8,subQ7,subQ6,subQ5,subQ4,subQ3,subQ2,subQ1,subQ0,subQ22,subQ23])],"isStart":false})})]});}
            var Q19;
            Q19=makeQuery(id+"F1.opExtrude","CAP_EDGE",EDGE,{"disambiguationData":[OSD([sQuery(id+"F0.wireOp",EDGE,"E16.MirrorCS")])],"isStart":true});
            var Q20;
            Q20=makeQuery(id+"F1.opExtrude","CAP_EDGE",EDGE,{"disambiguationData":[OSD([sQuery(id+"F0.wireOp",EDGE,"E14.MirrorCS")])],"isStart":false});
            var Q21;
            {var subQ0=sQuery(id+"F0.wireOp",EDGE,"E21.2.1");var subQ1=sQuery(id+"F0.wireOp",EDGE,"E21.2.0");var subQ2=sQuery(id+"F0.wireOp",EDGE,"E21.1.1");var subQ3=sQuery(id+"F0.wireOp",EDGE,"E21.1.0");var subQ4=sQuery(id+"F0.wireOp",EDGE,"E20");var subQ5=sQuery(id+"F0.wireOp",EDGE,"E19");var subQ6=sQuery(id+"F0.wireOp",EDGE,"E18.MirrorCS");var subQ7=sQuery(id+"F0.wireOp",EDGE,"E17.MirrorCS");var subQ8=sQuery(id+"F0.wireOp",EDGE,"E16.MirrorCS");var subQ9=sQuery(id+"F0.wireOp",EDGE,"E15.MirrorCS");var subQ10=sQuery(id+"F0.wireOp",EDGE,"E14.MirrorCS");var subQ11=sQuery(id+"F0.wireOp",EDGE,"E13.MirrorCS");var subQ12=sQuery(id+"F0.wireOp",EDGE,"E8");var subQ13=sQuery(id+"F0.wireOp",EDGE,"E7");var subQ14=sQuery(id+"F0.wireOp",EDGE,"E6");var subQ15=sQuery(id+"F0.wireOp",EDGE,"E5");var subQ16=sQuery(id+"F0.wireOp",EDGE,"E10.bottom");var subQ17=sQuery(id+"F0.wireOp",EDGE,"E10.top");var subQ18=sQuery(id+"F0.wireOp",EDGE,"E10.left");var subQ19=sQuery(id+"F0.wireOp",EDGE,"E10.right");var subQ20=sQuery(id+"F0.wireOp",EDGE,"E11");var subQ21=sQuery(id+"F0.wireOp",EDGE,"E12");var subQ22=sQuery(id+"F0.wireOp",EDGE,"E21.3.0");var subQ23=sQuery(id+"F0.wireOp",EDGE,"E21.3.1");Q21=makeQuery(id+"F4.opFillet","BLEND_EDGE",EDGE,{"blendedFrom":[makeQuery(id+"F1.opExtrude","SWEPT_EDGE",EDGE,{"disambiguationData":[OSD([subQ10,subQ4])]}),makeQuery(id+"F3.boolean.opBoolean","SPLIT",FACE,{"disambiguationData":[TD([makeQuery(id+"F1.opExtrude","SWEPT_FACE",FACE,{"disambiguationData":[OSD([subQ15])]})])],"derivedFrom":makeQuery(id+"F1.opExtrude","CAP_FACE",FACE,{"disambiguationData":[OSD([sQuery(id+"F0.wireOp",EDGE,"E1"),sQuery(id+"F0.wireOp",EDGE,"E2"),sQuery(id+"F0.wireOp",EDGE,"E3"),sQuery(id+"F0.wireOp",EDGE,"E4"),subQ15,subQ14,subQ13,subQ12,subQ16,subQ17,subQ18,subQ19,subQ20,subQ21,subQ11,subQ10,subQ9,subQ8,subQ7,subQ6,subQ5,subQ4,subQ3,subQ2,subQ1,subQ0,subQ22,subQ23])],"isStart":false})})],"blendedInto":[makeQuery(id+"F3.boolean.opBoolean","SPLIT",FACE,{"disambiguationData":[TD([makeQuery(id+"F1.opExtrude","SWEPT_FACE",FACE,{"disambiguationData":[OSD([subQ15])]})])],"derivedFrom":makeQuery(id+"F1.opExtrude","CAP_FACE",FACE,{"disambiguationData":[OSD([sQuery(id+"F0.wireOp",EDGE,"E1"),sQuery(id+"F0.wireOp",EDGE,"E2"),sQuery(id+"F0.wireOp",EDGE,"E3"),sQuery(id+"F0.wireOp",EDGE,"E4"),subQ15,subQ14,subQ13,subQ12,subQ16,subQ17,subQ18,subQ19,subQ20,subQ21,subQ11,subQ10,subQ9,subQ8,subQ7,subQ6,subQ5,subQ4,subQ3,subQ2,subQ1,subQ0,subQ22,subQ23])],"isStart":false})})]});}
            var Q22;
            Q22=makeQuery(id+"F1.opExtrude","CAP_EDGE",EDGE,{"disambiguationData":[OSD([sQuery(id+"F0.wireOp",EDGE,"E14.MirrorCS")])],"isStart":true});
            var Q23;
            {var subQ0=sQuery(id+"F0.wireOp",EDGE,"E20");var subQ1=sQuery(id+"F0.wireOp",EDGE,"E14.MirrorCS");Q23=makeQuery(id+"F4.opFillet","BLEND_EDGE",EDGE,{"blendedFrom":[makeQuery(id+"F1.opExtrude","SWEPT_EDGE",EDGE,{"disambiguationData":[OSD([subQ1,subQ0])]}),makeQuery(id+"F1.opExtrude","CAP_FACE",FACE,{"disambiguationData":[OSD([sQuery(id+"F0.wireOp",EDGE,"E1"),sQuery(id+"F0.wireOp",EDGE,"E2"),sQuery(id+"F0.wireOp",EDGE,"E3"),sQuery(id+"F0.wireOp",EDGE,"E4"),sQuery(id+"F0.wireOp",EDGE,"E5"),sQuery(id+"F0.wireOp",EDGE,"E6"),sQuery(id+"F0.wireOp",EDGE,"E7"),sQuery(id+"F0.wireOp",EDGE,"E8"),sQuery(id+"F0.wireOp",EDGE,"E10.bottom"),sQuery(id+"F0.wireOp",EDGE,"E10.top"),sQuery(id+"F0.wireOp",EDGE,"E10.left"),sQuery(id+"F0.wireOp",EDGE,"E10.right"),sQuery(id+"F0.wireOp",EDGE,"E11"),sQuery(id+"F0.wireOp",EDGE,"E12"),sQuery(id+"F0.wireOp",EDGE,"E13.MirrorCS"),subQ1,sQuery(id+"F0.wireOp",EDGE,"E15.MirrorCS"),sQuery(id+"F0.wireOp",EDGE,"E16.MirrorCS"),sQuery(id+"F0.wireOp",EDGE,"E17.MirrorCS"),sQuery(id+"F0.wireOp",EDGE,"E18.MirrorCS"),sQuery(id+"F0.wireOp",EDGE,"E19"),subQ0,sQuery(id+"F0.wireOp",EDGE,"E21.1.0"),sQuery(id+"F0.wireOp",EDGE,"E21.1.1"),sQuery(id+"F0.wireOp",EDGE,"E21.2.0"),sQuery(id+"F0.wireOp",EDGE,"E21.2.1"),sQuery(id+"F0.wireOp",EDGE,"E21.3.0"),sQuery(id+"F0.wireOp",EDGE,"E21.3.1")])],"isStart":true})],"blendedInto":[makeQuery(id+"F1.opExtrude","CAP_FACE",FACE,{"disambiguationData":[OSD([sQuery(id+"F0.wireOp",EDGE,"E1"),sQuery(id+"F0.wireOp",EDGE,"E2"),sQuery(id+"F0.wireOp",EDGE,"E3"),sQuery(id+"F0.wireOp",EDGE,"E4"),sQuery(id+"F0.wireOp",EDGE,"E5"),sQuery(id+"F0.wireOp",EDGE,"E6"),sQuery(id+"F0.wireOp",EDGE,"E7"),sQuery(id+"F0.wireOp",EDGE,"E8"),sQuery(id+"F0.wireOp",EDGE,"E10.bottom"),sQuery(id+"F0.wireOp",EDGE,"E10.top"),sQuery(id+"F0.wireOp",EDGE,"E10.left"),sQuery(id+"F0.wireOp",EDGE,"E10.right"),sQuery(id+"F0.wireOp",EDGE,"E11"),sQuery(id+"F0.wireOp",EDGE,"E12"),sQuery(id+"F0.wireOp",EDGE,"E13.MirrorCS"),subQ1,sQuery(id+"F0.wireOp",EDGE,"E15.MirrorCS"),sQuery(id+"F0.wireOp",EDGE,"E16.MirrorCS"),sQuery(id+"F0.wireOp",EDGE,"E17.MirrorCS"),sQuery(id+"F0.wireOp",EDGE,"E18.MirrorCS"),sQuery(id+"F0.wireOp",EDGE,"E19"),subQ0,sQuery(id+"F0.wireOp",EDGE,"E21.1.0"),sQuery(id+"F0.wireOp",EDGE,"E21.1.1"),sQuery(id+"F0.wireOp",EDGE,"E21.2.0"),sQuery(id+"F0.wireOp",EDGE,"E21.2.1"),sQuery(id+"F0.wireOp",EDGE,"E21.3.0"),sQuery(id+"F0.wireOp",EDGE,"E21.3.1")])],"isStart":true})]});}
            var Q24;
            Q24=makeQuery(id+"F1.opExtrude","CAP_EDGE",EDGE,{"disambiguationData":[OSD([sQuery(id+"F0.wireOp",EDGE,"E20")])],"isStart":true});
            fillet(context, id + "F7", {"entities" : qUnion([Q0, Q1, Q2, Q3, Q4, Q5, Q6, Q7, Q8, Q9, Q10, Q11, Q12, Q13, Q14, Q15, Q16, Q17, Q18, Q19, Q20, Q21, Q22, Q23, Q24]), "radius" : 1 * mm, "tangentPropagation" : true, "allowEdgeOverflow" : false});
        }
        {
            var Q0;
            Q0=makeQuery(id+"F2.opExtrude","CAP_FACE",FACE,{"disambiguationData":[OSD([sQuery(id+"F0.wireOp",EDGE,"E4"),sQuery(id+"F0.wireOp",EDGE,"E6")])],"isStart":false});
            var Q1;
            Q1=makeQuery(id+"F2.opExtrude","CAP_EDGE",EDGE,{"disambiguationData":[OSD([sQuery(id+"F0.wireOp",EDGE,"E2")])],"isStart":false});
            var Q2;
            Q2=makeQuery(id+"F2.opExtrude","CAP_EDGE",EDGE,{"disambiguationData":[OSD([sQuery(id+"F0.wireOp",EDGE,"E8")])],"isStart":false});
            var Q3;
            Q3=makeQuery(id+"F2.opExtrude","CAP_EDGE",EDGE,{"disambiguationData":[OSD([sQuery(id+"F0.wireOp",EDGE,"E3")])],"isStart":false});
            var Q4;
            Q4=makeQuery(id+"F2.opExtrude","CAP_EDGE",EDGE,{"disambiguationData":[OSD([sQuery(id+"F0.wireOp",EDGE,"E7")])],"isStart":false});
            var Q5;
            Q5=makeQuery(id+"F2.opExtrude","CAP_EDGE",EDGE,{"disambiguationData":[OSD([sQuery(id+"F0.wireOp",EDGE,"E1")])],"isStart":false});
            var Q6;
            Q6=makeQuery(id+"F2.opExtrude","CAP_EDGE",EDGE,{"disambiguationData":[OSD([sQuery(id+"F0.wireOp",EDGE,"E5")])],"isStart":false});
            fillet(context, id + "F8", {"entities" : qUnion([Q0, Q1, Q2, Q3, Q4, Q5, Q6]), "radius" : 1 * mm, "tangentPropagation" : true, "allowEdgeOverflow" : false});
        }
    });
